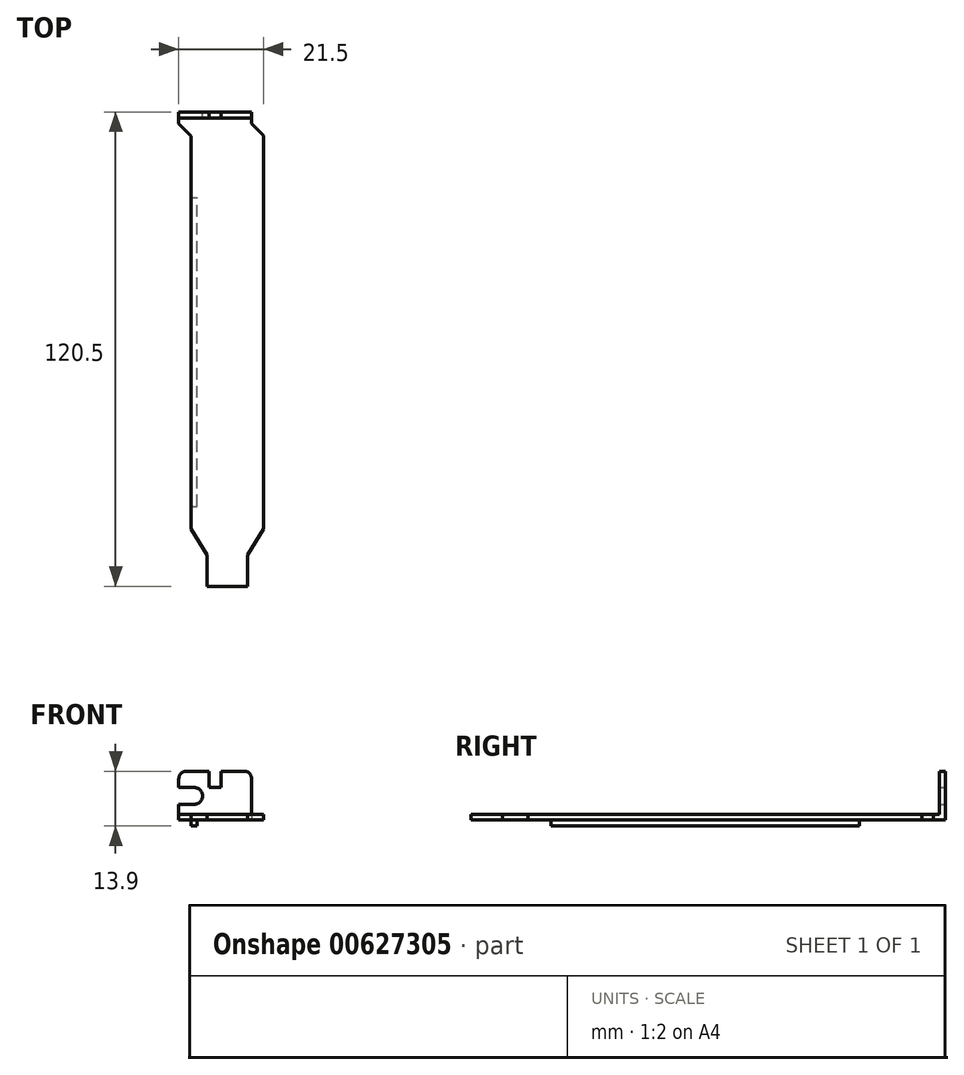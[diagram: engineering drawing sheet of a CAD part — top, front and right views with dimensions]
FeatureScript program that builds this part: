
annotation { "Feature Type Name" : "Feature", "Feature Type Description" : "" }
export const myFeature = defineFeature(function(context is Context, id is Id, definition is map)
    precondition{}
    {
        {
            var Q0;
            Q0=qCreatedBy(makeId("Top.planeOp"),FACE);
            var sketch = newSketch(context, id + "F0", { "sketchPlane" : qUnion([Q0])});
            skLineSegment(sketch, "E0", {"start": v(0, 99.9) * mm, "end": v(0, 0) * mm});
            skLineSegment(sketch, "E1", {"start": v(0, 0) * mm, "end": v(4.05, -6.5) * mm});
            skLineSegment(sketch, "E2", {"start": v(4.05, -6.5) * mm, "end": v(4.05, -14.5) * mm});
            skLineSegment(sketch, "E3", {"start": v(4.05, -14.5) * mm, "end": v(14.35, -14.5) * mm});
            skLineSegment(sketch, "E4", {"start": v(14.35, -14.5) * mm, "end": v(14.35, -6.5) * mm});
            skLineSegment(sketch, "E5", {"start": v(14.35, -6.5) * mm, "end": v(18.4, 0) * mm});
            skLineSegment(sketch, "E6", {"start": v(18.4, 0) * mm, "end": v(18.4, 100) * mm});
            skLineSegment(sketch, "E7", {"start": v(18.4, 100) * mm, "end": v(15.4, 103) * mm});
            skLineSegment(sketch, "E8", {"start": v(15.4, 103) * mm, "end": v(15.4, 106) * mm});
            skLineSegment(sketch, "E9", {"start": v(15.4, 106) * mm, "end": v(-3.1, 106) * mm});
            skLineSegment(sketch, "E10", {"start": v(-3.1, 106) * mm, "end": v(-3.1, 103) * mm});
            skLineSegment(sketch, "E11", {"start": v(-3.1, 103) * mm, "end": v(0, 99.9) * mm});
            skLineSegment(sketch, "E12", {"start": v(0, 0) * mm, "end": v(18.4, 0) * mm, "construction": true});
            skLineSegment(sketch, "E13", {"start": v(9.2, 0) * mm, "end": v(9.2, -14.5) * mm, "construction": true});
            skSolve(sketch);
        }
        {
            var Q0;
            Q0=makeQuery(id+"F0.imprint","IMPRINT",FACE,{"disambiguationData":[TD([[makeQuery(id+"F0.imprint","IMPRINT",EDGE,{"derivedFrom":sQuery(id+"F0.wireOp",EDGE,"E0")}),1.0]])]});
            extrude(context, id + "F1", {"entities" : qUnion([Q0]), "depth" : 1.5 * mm, "offsetDistance" : 25 * mm});
        }
        {
            var Q0;
            Q0=makeQuery(id+"F1.opExtrude","CAP_FACE",FACE,{"disambiguationData":[OSD([sQuery(id+"F0.wireOp",EDGE,"E0"),sQuery(id+"F0.wireOp",EDGE,"E1"),sQuery(id+"F0.wireOp",EDGE,"E2"),sQuery(id+"F0.wireOp",EDGE,"E3"),sQuery(id+"F0.wireOp",EDGE,"E4"),sQuery(id+"F0.wireOp",EDGE,"E5"),sQuery(id+"F0.wireOp",EDGE,"E6"),sQuery(id+"F0.wireOp",EDGE,"E7"),sQuery(id+"F0.wireOp",EDGE,"E8"),sQuery(id+"F0.wireOp",EDGE,"E9"),sQuery(id+"F0.wireOp",EDGE,"E10"),sQuery(id+"F0.wireOp",EDGE,"E11")])],"isStart":false});
            var sketch = newSketch(context, id + "F2", { "sketchPlane" : qUnion([Q0])});
            skLineSegment(sketch, "E14.bottom", {"start": v(-3.1, 106) * mm, "end": v(15.4, 106) * mm});
            skLineSegment(sketch, "E14.top", {"start": v(-3.1, 104.5) * mm, "end": v(15.4, 104.5) * mm});
            skLineSegment(sketch, "E14.left", {"start": v(-3.1, 106) * mm, "end": v(-3.1, 104.5) * mm});
            skLineSegment(sketch, "E14.right", {"start": v(15.4, 106) * mm, "end": v(15.4, 104.5) * mm});
            skSolve(sketch);
        }
        {
            var Q0;
            Q0 = qSketchRegion(id + "F2", true);
            extrude(context, id + "F3", {"entities" : qUnion([Q0]), "operationType" : NewBodyOperationType.ADD, "depth" : (12.4 - 1.5) * mm, "offsetDistance" : 25 * mm});
        }
        {
            var Q0;
            Q0=makeQuery(id+"F3.boolean.opBoolean","MERGE",FACE,{"derivedFrom":[makeQuery(id+"F1.opExtrude","SWEPT_FACE",FACE,{"disambiguationData":[OSD([sQuery(id+"F0.wireOp",EDGE,"E9")])]}),makeQuery(id+"F3.opExtrude","SWEPT_FACE",FACE,{"disambiguationData":[OSD([sQuery(id+"F2.wireOp",EDGE,"E14.bottom")])]})]});
            var sketch = newSketch(context, id + "F4", { "sketchPlane" : qUnion([Q0])});
            skLineSegment(sketch, "E15", {"start": v(-7.68, 12.4) * mm, "end": v(-7.68, 8.3) * mm});
            skLineSegment(sketch, "E16", {"start": v(-7.68, 8.3) * mm, "end": v(-4.63, 8.3) * mm});
            skLineSegment(sketch, "E17", {"start": v(-4.63, 8.3) * mm, "end": v(-4.63, 12.4) * mm});
            skLineSegment(sketch, "E18", {"start": v(-4.63, 12.4) * mm, "end": v(-7.68, 12.4) * mm});
            skLineSegment(sketch, "E19", {"start": v(-6.15, 0) * mm, "end": v(-6.15, 8.3) * mm, "construction": true});
            skArc(sketch, "E20", {"start": v(-13.5, 12.4) * mm, "mid": v(-14.84, 11.84) * mm, "end": v(-15.4, 10.5) * mm});
            skLineSegment(sketch, "E21", {"start": v(-15.4, 10.5) * mm, "end": v(-15.4, 12.4) * mm});
            skLineSegment(sketch, "E22", {"start": v(-15.4, 12.4) * mm, "end": v(-13.5, 12.4) * mm});
            skLineSegment(sketch, "E23", {"start": v(1.2, 12.4) * mm, "end": v(3.1, 12.4) * mm});
            skLineSegment(sketch, "E24", {"start": v(3.1, 12.4) * mm, "end": v(3.1, 10.5) * mm});
            skArc(sketch, "E25", {"start": v(1.2, 12.4) * mm, "mid": v(2.54, 11.84) * mm, "end": v(3.1, 10.5) * mm});
            skLineSegment(sketch, "E26", {"start": v(-0.81, 8.26) * mm, "end": v(3.1, 8.26) * mm});
            skLineSegment(sketch, "E27", {"start": v(3.1, 8.26) * mm, "end": v(3.1, 4) * mm});
            skLineSegment(sketch, "E28", {"start": v(3.1, 4) * mm, "end": v(-0.81, 4) * mm});
            skArc(sketch, "E29", {"start": v(-0.81, 8.26) * mm, "mid": v(-2.94, 6.13) * mm, "end": v(-0.81, 4) * mm});
            skSolve(sketch);
        }
        {
            var Q0;
            Q0 = qSketchRegion(id + "F4", true);
            extrude(context, id + "F5", {"entities" : qUnion([Q0]), "operationType" : NewBodyOperationType.REMOVE, "oppositeDirection" : true, "depth" : 25 * mm, "offsetDistance" : 25 * mm});
        }
        {
            var Q0;
            Q0=makeQuery(id+"F1.opExtrude","CAP_FACE",FACE,{"disambiguationData":[OSD([sQuery(id+"F0.wireOp",EDGE,"E0"),sQuery(id+"F0.wireOp",EDGE,"E1"),sQuery(id+"F0.wireOp",EDGE,"E2"),sQuery(id+"F0.wireOp",EDGE,"E3"),sQuery(id+"F0.wireOp",EDGE,"E4"),sQuery(id+"F0.wireOp",EDGE,"E5"),sQuery(id+"F0.wireOp",EDGE,"E6"),sQuery(id+"F0.wireOp",EDGE,"E7"),sQuery(id+"F0.wireOp",EDGE,"E8"),sQuery(id+"F0.wireOp",EDGE,"E9"),sQuery(id+"F0.wireOp",EDGE,"E10"),sQuery(id+"F0.wireOp",EDGE,"E11")])],"isStart":true});
            var sketch = newSketch(context, id + "F6", { "sketchPlane" : qUnion([Q0])});
            skLineSegment(sketch, "E30.bottom", {"start": v(0, -5.8) * mm, "end": v(1.5, -5.8) * mm});
            skLineSegment(sketch, "E30.top", {"start": v(0, -84.2) * mm, "end": v(1.5, -84.2) * mm});
            skLineSegment(sketch, "E30.left", {"start": v(0, -5.8) * mm, "end": v(0, -84.2) * mm});
            skLineSegment(sketch, "E30.right", {"start": v(1.5, -5.8) * mm, "end": v(1.5, -84.2) * mm});
            skSolve(sketch);
        }
        {
            var Q0;
            Q0 = qSketchRegion(id + "F6", true);
            extrude(context, id + "F7", {"entities" : qUnion([Q0]), "operationType" : NewBodyOperationType.ADD, "depth" : 1.5 * mm, "offsetDistance" : 25 * mm});
        }
    });
